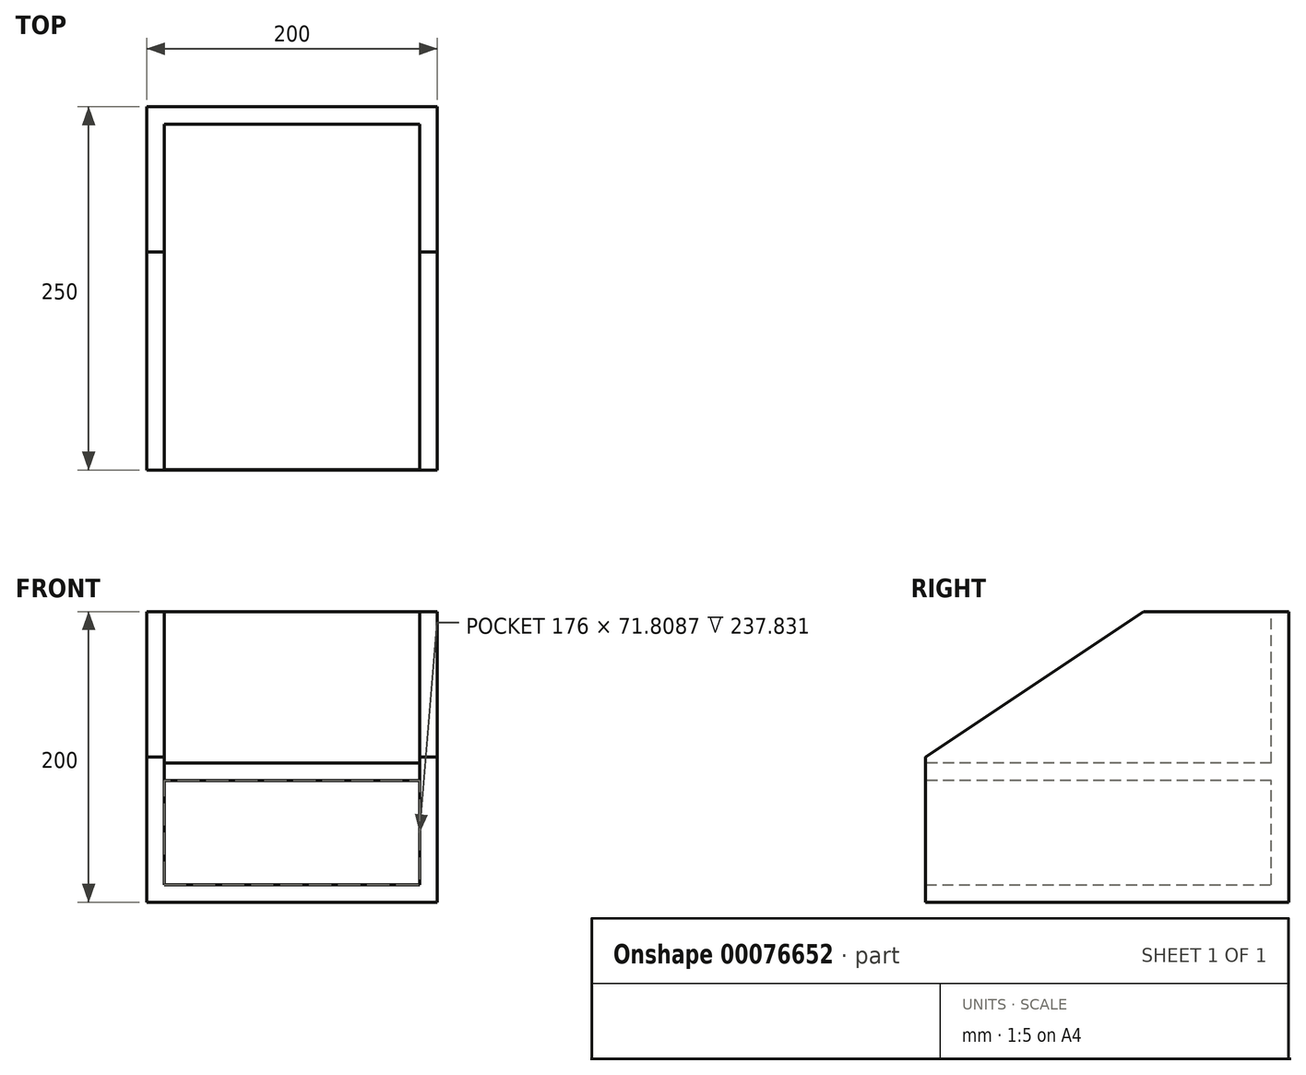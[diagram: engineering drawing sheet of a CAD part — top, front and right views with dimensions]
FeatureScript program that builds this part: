
annotation { "Feature Type Name" : "Feature", "Feature Type Description" : "" }
export const myFeature = defineFeature(function(context is Context, id is Id, definition is map)
    precondition{}
    {
        {
            var Q0;
            Q0=qCreatedBy(makeId("Right.planeOp"),FACE);
            var sketch = newSketch(context, id + "F0", { "sketchPlane" : qUnion([Q0])});
            skLineSegment(sketch, "E0", {"start": v(-55.1, -155.8) * mm, "end": v(194.9, -155.8) * mm});
            skLineSegment(sketch, "E1", {"start": v(194.9, -155.8) * mm, "end": v(194.9, 44.2) * mm});
            skLineSegment(sketch, "E2", {"start": v(194.9, 44.2) * mm, "end": v(94.9, 44.2) * mm});
            skLineSegment(sketch, "E3", {"start": v(94.9, 44.2) * mm, "end": v(-55.1, -55.8) * mm});
            skLineSegment(sketch, "E4", {"start": v(-55.1, -55.8) * mm, "end": v(-55.1, -155.8) * mm});
            skSolve(sketch);
        }
        {
            var Q0;
            Q0=makeQuery(id+"F0.imprint","IMPRINT",FACE,{"disambiguationData":[TD([[makeQuery(id+"F0.imprint","IMPRINT",EDGE,{"derivedFrom":sQuery(id+"F0.wireOp",EDGE,"E0")}),1.0]])]});
            extrude(context, id + "F1", {"entities" : qUnion([Q0]), "endBound" : BoundingType.SYMMETRIC, "depth" : 200 * mm});
        }
        {
            var Q0;
            Q0=makeQuery(id+"F1.opExtrude","SWEPT_FACE",FACE,{"disambiguationData":[OSD([sQuery(id+"F0.wireOp",EDGE,"E2")])]});
            var Q1;
            Q1=makeQuery(id+"F1.opExtrude","SWEPT_FACE",FACE,{"disambiguationData":[OSD([sQuery(id+"F0.wireOp",EDGE,"E3")])]});
            var Q2;
            Q2=makeQuery(id+"F1.opExtrude","SWEPT_FACE",FACE,{"disambiguationData":[OSD([sQuery(id+"F0.wireOp",EDGE,"E4")])]});
            shell(context, id + "F2", {"entities" : qUnion([Q0, Q1, Q2]), "thickness" : 12 * mm});
        }
        {
            var Q0;
            Q0=qCreatedBy(makeId("Top.planeOp"),FACE);
            cPlane(context, id + "F3", {"entities" : qUnion([Q0]), "cplaneType" : CPlaneType.OFFSET, "offset" : 60 * mm, "oppositeDirection" : true, "width" : 150 * mm, "height" : 150 * mm});
        }
        {
            var Q0;
            Q0=qCreatedBy(id+"F3.planeOp",FACE);
            var sketch = newSketch(context, id + "F4", { "sketchPlane" : qUnion([Q0])});
            skLineSegment(sketch, "E5.bottom", {"start": v(-90.58, 186.88) * mm, "end": v(91.75, 186.88) * mm});
            skLineSegment(sketch, "E5.top", {"start": v(-90.58, -54.92) * mm, "end": v(91.75, -54.92) * mm});
            skLineSegment(sketch, "E5.left", {"start": v(-90.58, 186.88) * mm, "end": v(-90.58, -54.92) * mm});
            skLineSegment(sketch, "E5.right", {"start": v(91.75, 186.88) * mm, "end": v(91.75, -54.92) * mm});
            skSolve(sketch);
        }
        {
            var Q0;
            Q0=makeQuery(id+"F4.imprint","IMPRINT",FACE,{"disambiguationData":[TD([[makeQuery(id+"F4.imprint","IMPRINT",EDGE,{"derivedFrom":sQuery(id+"F4.wireOp",EDGE,"E5.bottom")}),-1.0]])]});
            extrude(context, id + "F5", {"entities" : qUnion([Q0]), "operationType" : NewBodyOperationType.ADD, "oppositeDirection" : true, "depth" : 12 * mm});
        }
    });
